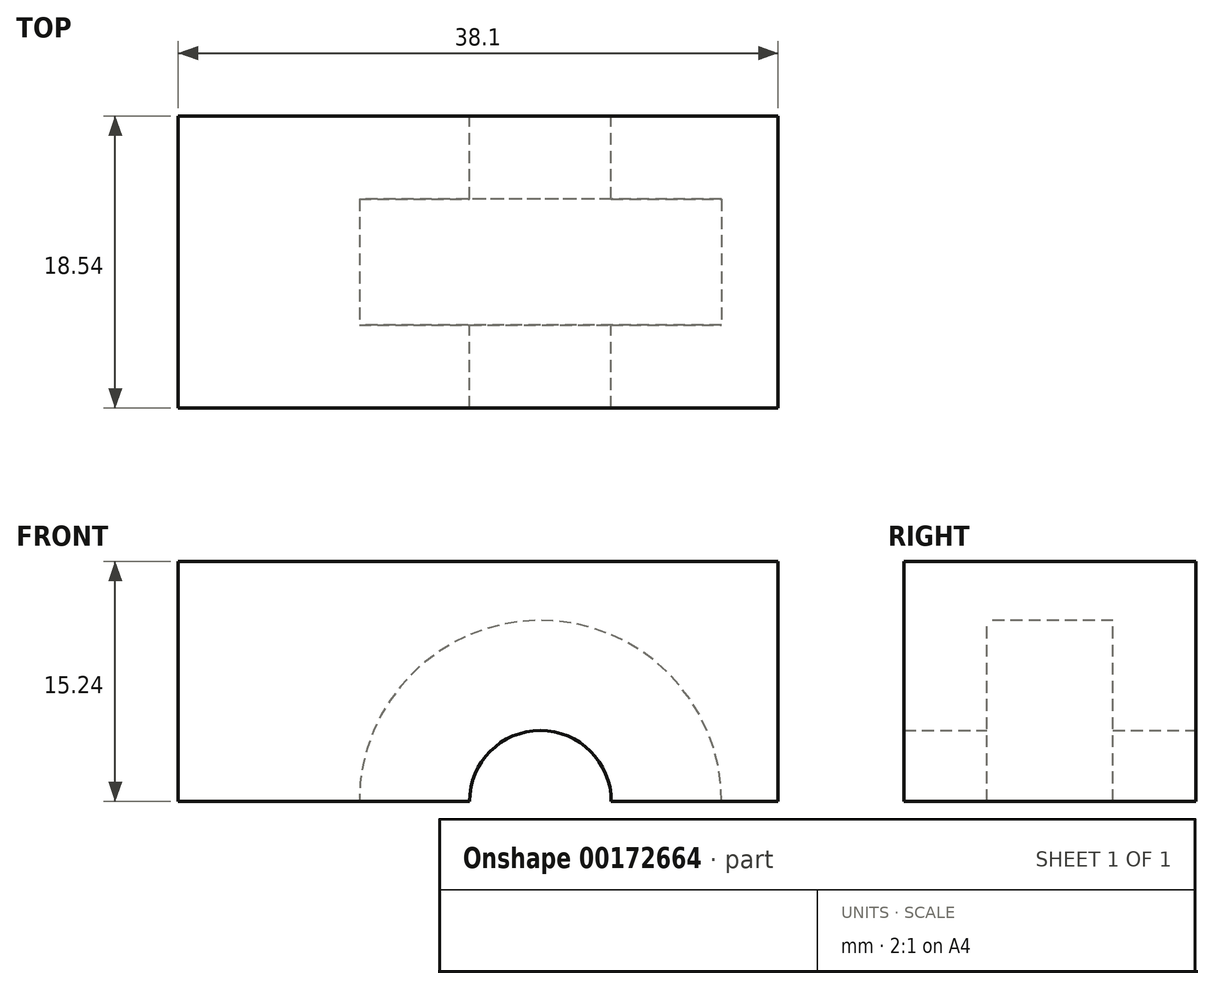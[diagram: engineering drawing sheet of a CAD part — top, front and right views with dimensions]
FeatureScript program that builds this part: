
annotation { "Feature Type Name" : "Feature", "Feature Type Description" : "" }
export const myFeature = defineFeature(function(context is Context, id is Id, definition is map)
    precondition{}
    {
        {
            var Q0;
            Q0=qCreatedBy(makeId("Top.planeOp"),FACE);
            var sketch = newSketch(context, id + "F0", { "sketchPlane" : qUnion([Q0])});
            skLineSegment(sketch, "E0.bottom", {"start": v(19.05, 9.27) * mm, "end": v(-19.05, 9.27) * mm});
            skLineSegment(sketch, "E0.top", {"start": v(19.05, -9.27) * mm, "end": v(-19.05, -9.27) * mm});
            skLineSegment(sketch, "E0.left", {"start": v(19.05, 9.27) * mm, "end": v(19.05, -9.27) * mm});
            skLineSegment(sketch, "E0.right", {"start": v(-19.05, 9.27) * mm, "end": v(-19.05, -9.27) * mm});
            skPoint(sketch, "E0.middle", {"position": v(0, 0) * mm});
            skLineSegment(sketch, "E1", {"start": v(-19.05, 0) * mm, "end": v(19.05, 0) * mm, "construction": true});
            skLineSegment(sketch, "E2", {"start": v(-19.05, -4) * mm, "end": v(19.05, -4) * mm});
            skSolve(sketch);
        }
        {
            var Q0;
            {var subQ0=sQuery(id+"F0.wireOp",EDGE,"E0.bottom");Q0=makeQuery(id+"F0.imprint","IMPRINT",FACE,{"disambiguationData":[TD([[makeQuery(id+"F0.imprint","IMPRINT",EDGE,{"derivedFrom":subQ0}),1.0]])]});}
            extrude(context, id + "F1", {"entities" : qUnion([Q0]), "depth" : 15.24 * mm});
        }
        {
            var Q0;
            Q0=makeQuery(id+"F1.opExtrude","SWEPT_FACE",FACE,{"disambiguationData":[OSD([sQuery(id+"F0.wireOp",EDGE,"E2")])]});
            var sketch = newSketch(context, id + "F2", { "sketchPlane" : qUnion([Q0])});
            skCircle(sketch, "E3", {"center": v(3.95, 0) * mm, "radius": 11.5 * mm});
            skCircle(sketch, "E4", {"center": v(3.95, 0) * mm, "radius": 4.5 * mm});
            skSolve(sketch);
        }
        {
            var Q0;
            {var subQ0=sQuery(id+"F2.wireOp",EDGE,"E3");var subQ1=makeQuery(id+"F1.opExtrude","CAP_EDGE",EDGE,{"disambiguationData":[OSD([sQuery(id+"F0.wireOp",EDGE,"E2")])],"isStart":true});var subQ2=makeQuery(id+"F2.imprint","INTERSECT",VERTEX,{"disambiguationData":[OD(0.0)],"derivedFrom":[subQ1,subQ0]});Q0=makeQuery(id+"F2.imprint","IMPRINT",FACE,{"disambiguationData":[TD([[makeQuery(id+"F2.imprint","IMPRINT",EDGE,{"disambiguationData":[TD([[subQ2,1.0]])],"derivedFrom":subQ0}),1.0]])]});}
            var Q1;
            {var subQ0=sQuery(id+"F2.wireOp",EDGE,"E4");var subQ1=makeQuery(id+"F1.opExtrude","CAP_EDGE",EDGE,{"disambiguationData":[OSD([sQuery(id+"F0.wireOp",EDGE,"E2")])],"isStart":true});var subQ2=makeQuery(id+"F2.imprint","INTERSECT",VERTEX,{"disambiguationData":[OD(0.0)],"derivedFrom":[subQ1,subQ0]});Q1=makeQuery(id+"F2.imprint","IMPRINT",FACE,{"disambiguationData":[TD([[makeQuery(id+"F2.imprint","IMPRINT",EDGE,{"disambiguationData":[TD([[subQ2,1.0]])],"derivedFrom":subQ0}),1.0]])]});}
            extrude(context, id + "F3", {"entities" : qUnion([Q0, Q1]), "operationType" : NewBodyOperationType.REMOVE, "oppositeDirection" : true, "depth" : 8 * mm});
        }
        {
            var Q0;
            {var subQ0=sQuery(id+"F0.wireOp",EDGE,"E0.top");Q0=makeQuery(id+"F0.imprint","IMPRINT",FACE,{"disambiguationData":[TD([[makeQuery(id+"F0.imprint","IMPRINT",EDGE,{"derivedFrom":subQ0}),-1.0]])]});}
            extrude(context, id + "F4", {"entities" : qUnion([Q0]), "operationType" : NewBodyOperationType.ADD, "depth" : 15.24 * mm});
        }
        {
            var Q0;
            Q0=makeQuery(id+"F1.opExtrude","SWEPT_FACE",FACE,{"disambiguationData":[OSD([sQuery(id+"F0.wireOp",EDGE,"E0.bottom")])]});
            var sketch = newSketch(context, id + "F5", { "sketchPlane" : qUnion([Q0])});
            skCircle(sketch, "E5", {"center": v(-3.95, 0) * mm, "radius": 4.5 * mm});
            skSolve(sketch);
        }
        {
            var Q0;
            Q0 = qSketchRegion(id + "F5", true);
            extrude(context, id + "F6", {"entities" : qUnion([Q0]), "operationType" : NewBodyOperationType.REMOVE, "oppositeDirection" : true, "depth" : 50.8 * mm});
        }
    });
